# Revit family: QF_ELECTROLUXPROFESSIONAL_589932_HCLDBBJODM
name_source: partatom
category: Specialty Equipment
units: mm (PartAtom-declared; Revit-internal decimal feet)

## family parameters
Always vertical = Yes
Cut with Voids When Loaded = No
Enable Cutting in Views = No
Maintain Annotation Orientation = No
Part Type = Normal
Room Calculation Point = No
Round Connector Dimension = Use Diameter
Shared = No
Work Plane-Based = No

## types (1)
- QF_ELECTROLUXPROFESSIONAL_589932_HCLDBBJODM
    Accessory = No
    Cycle = 60 Hz
    Default Elevation = 0 mm  [stored 0 ft]
    Depth Actual = 900 mm  [stored 2.95276 ft]
    Description = EL. SOLID TOP, 4 ZONES, ECO, 1-SIDE, SPLASHBACK, 1000X900X250H MARINE USPHS (ONLY M2M)
    Gas KW = 0
    HP = 21.5 HP
    Height Actual = 250 mm  [stored 0.82021 ft]
    Length Actual = 1000 mm  [stored 3.28084 ft]
    Manufacturer = Electrolux Professional
    Model = HCLDBBJODM
    Phase = 3
    URL = http://www.electroluxprofessional.com
    URL Manufacturer = http://www.electroluxprofessional.com
    Volts = 440 V
    Watts = 0 W
    Weight = 170.00 kg
    Weight in Pounds = 0

note: [stored X ft] marks values corroborated as IEEE doubles in the binary element streams (Revit-internal decimal feet)

## geometry (parser evidence)
native form markers: Blend x12, Sweep x19
no freeform markers — native parametric forms only
